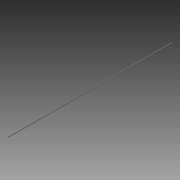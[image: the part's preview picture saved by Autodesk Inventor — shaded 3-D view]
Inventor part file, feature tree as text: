
AUTODESK INVENTOR PART (.ipt)
format: ipt  version: 2013 (Build 170138000, 138)  size: 84,480 bytes
history: native  units: in
note: dims shown in document units (in); Inventor stores cm internally (conversion verified against a paired STEP export)
features: other x2, plane x1, extrude x1, sketch x1
ambient origin geometry x8: Origin, YZ Plane, XZ Plane, XY Plane, X Axis, Y Axis, Z Axis, Center Point
feature tree (5):
  other  "Table"
  other  "vee-track-01"
  plane  "Work Plane1"
  extrude  "Extrusion1"  [1 undecoded]
  sketch  "Sketch1"  dims[d1=0.0in]
note: 1 required parameter value undecoded (feature->parameter linkage not recoverable at this tier; creation-order binding heuristic only, values carry confidence <= 0.55)
